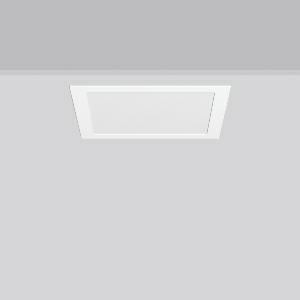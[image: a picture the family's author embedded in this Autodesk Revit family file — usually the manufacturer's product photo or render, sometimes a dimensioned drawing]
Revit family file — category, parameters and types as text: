
# Revit family: toledo_flat_square_e_672239_002_1_a966
name_source: partatom
category: Lighting Fixtures
units: mm (PartAtom-declared; Revit-internal decimal feet)

## family parameters
Cut with Voids When Loaded = No
Host = Face
Light Source = No
Part Type = Normal
Room Calculation Point = No
Round Connector Dimension = Use Diameter
Shared = No

## types (1)
- TOLEDO FLAT square E (1 x LED Modul 840, 2200 lm, 4000)
    Apparent Load = 25 VA
    CIE Flux Codes = 49 80 96 100 100
    Color Rendering = 80
    Color Temperature = 4000
    Default Elevation = 1800 mm
    Description = Series: TOLEDO FLAT square
Square recessed downlight. For escape route illumination. Housing: die-cast aluminium, powder-coated. Lightguide and diffuser made of non-yellowing plastic (PMMA). Diffuser opal matt plastic. Ceiling installation with spring system. Including separate LED converter with connecting cable 250 mm. Self-contained system with automatic self-test. External driver with simple plug-in locking system. 
Colour: white
Length: 300 mm
Width: 300 mm
Height: 3 mm
Cut-out length: 280 mm
Cut-out width: 280 mm
Recess height: 90 mm
Luminaire: recess height: 60-80 mm
Weight: 2.23 kg
Operating mode: maintained power mode
Duration time: 3 h
Lamp: LED
Socket: without socket
Colour temperature: 4000K
Colour rendering index (CRI): 80
System power: 25 W
Rated luminous flux: 2200 lm
Luminous flux, emergency: 430 lm
System power, emergency: -
Control gear: Regulated power supply
Protection class: I
Type of protection: IP 54
    Height = 0 mm  [stored 0 ft]
    Lamp = 1 x LED Modul 840
    Lamp Light Flux = 2200 lm
    Lamp count = 1
    Length = 300 mm
    Lifetime = 50000 h
    Luminous efficacy = 88 lm/W
    Manufacturer = RZB
    ModVariant = No
    Model = 672239.002.1
    Mounting Place = Ceiling
    Mounting Type = Recessed
    Number of Poles = 1
    OnlyDefault = Yes
    Power Factor = 1
    Product Name = TOLEDO FLAT square E
    Product group = Recessed downlights
    ProductGroupID = 402
    Protection Class = Protection class I
    Protection Degree = IP 40
    RLX_Detail_Level = 1
    RLX_Emergency_Light_Flux = 430 lm
    RLX_Emergency_Type = 3
    RLX_Emergency_Type_DB = Yes
    RlxData = <blob elided: 13213 chars, md5=3e8448da>
    Socket = socket
    Standby Power = 0 W
    System Light Flux = 2200 lm
    System Power = 25 W
    Type Comments = Product without accessories
    Type Image = 901488.002.jpg
    URL = http://relux.com
    VarID = ---
    Voltage = 0 V
    Weight = 0.00 kg
    Width = 300 mm

note: [stored X ft] marks values corroborated as IEEE doubles in the binary element streams (Revit-internal decimal feet)

## geometry (parser evidence)
native form markers: Sweep x7
no freeform markers — native parametric forms only
